# Revit family: Тактильная полиуретановая плитка диагональ(приклеивание)
name_source: partatom
category: Оборудование
revit_build: Autodesk Revit 2017 (Build: 20160225_1515(x64)
units: mm (PartAtom-declared; Revit-internal decimal feet)

## family parameters
Общий = Да
Основа = Грань
При загрузке вырезать с полостями = Да
Размер круглого соединителя = Использовать диаметр
Тип детали = Нормальный
Точка расчета площади = Нет

## types (2) — shared parameters
ADSK_Наименование = Тактильная плитка полиуретан диагональные полосы (приклеивание)
ADSK_Размер_Высота рифа = 5 мм
ADSK_Размер_Габариты = 300Х300
ADSK_Размер_Длина = 300 мм
ADSK_Размер_Толщина = 2 мм
ADSK_Размер_Ширина = 300 мм
ADSK_Тип рифов = Рельефные полосы
URL = http://tiflocentre.ru
Изготовитель = ТИФЛОЦЕНТР «ВЕРТИКАЛЬ»
Применение = Улица/Помещение
Стоимость = 175 $
zero-valued in all types: Отметка по умолчанию

## per-type parameters (varying)
| type | ADSK_Код изделия | ADSK_Материал наименование | ADSK_Материал плитки | Описание |
| Тактильная плитка полиуретан дагональ_Желтая | 10131-ZH | Полиуретан, цвет желтый | Вертикаль_Полиуретан_Желтый | Тактильная Полиуретановая (ПУ) плитка предназначена для обеспечения информирования при движении людей с ограничениями зрения. Диагональные рифы. Данная модель желтой тактильной ПУ плитки с диагональными рифами используется для указания смены движения незрячего человека.  Тактильная ПУ плитка монтируется к любой поверхности при помощи клея. |
| Тактильная плитка полиуретановая_Черная | 10128-CH | Полиуретан, цвет черный | Вертикаль_Полиуретан_Черный | Тактильная ПВХ плитка создана для обеспечения информирования при движении маломобильных групп населения. Применяется для размещения на пути следования внутри общественных объектов для адаптаци людей с ограничениями зрения. ПВХ плитка обладает отличным качеством и имеет черный цвет, контрастный к светлой поверхности. Тактильная ПВХ плитка от Тифлоцентра "Вертикаль" протестирована незрячими специалистами и рекомендована к применению ВОС, гос. программой "Доступная среда", выполнена плитка по (ГОСТ Р 56305-2014). |
